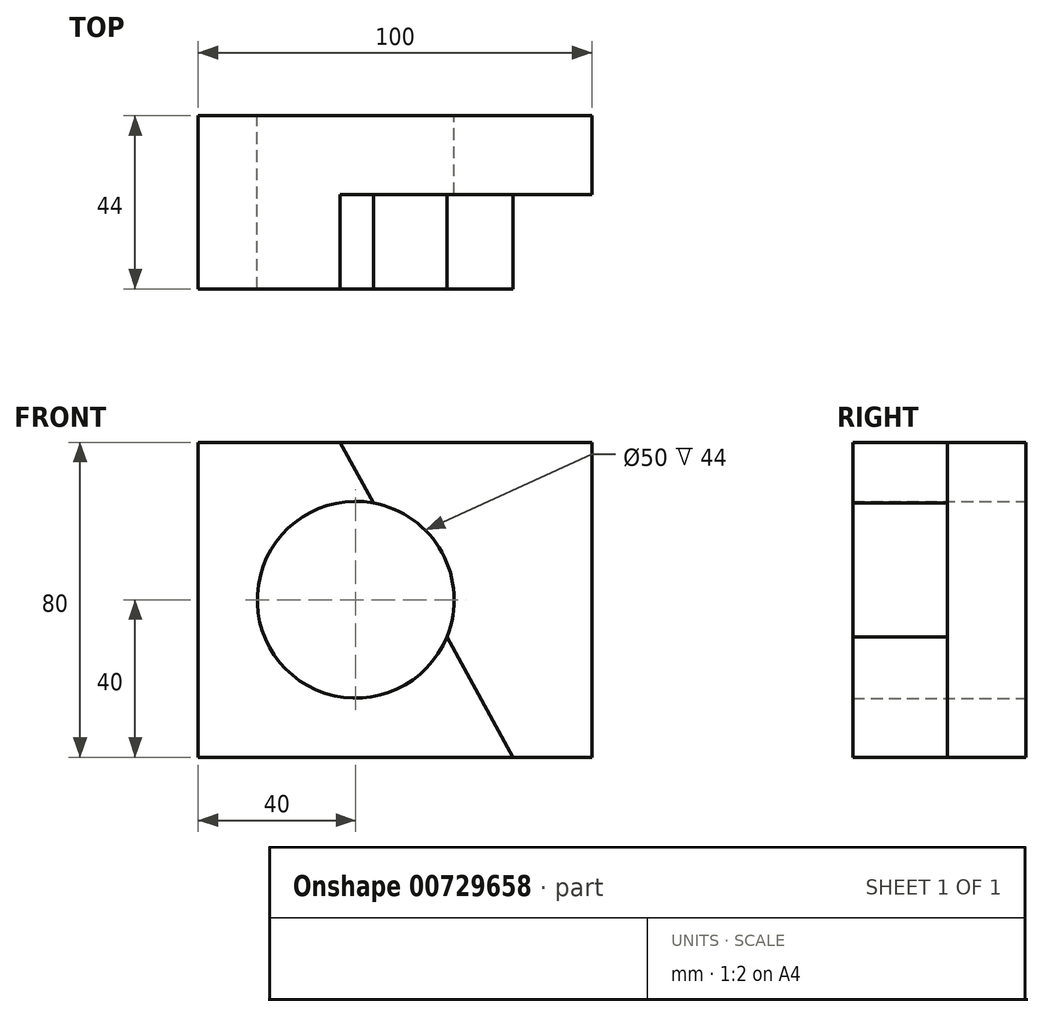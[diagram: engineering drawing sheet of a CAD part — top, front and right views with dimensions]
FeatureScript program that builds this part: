
annotation { "Feature Type Name" : "Feature", "Feature Type Description" : "" }
export const myFeature = defineFeature(function(context is Context, id is Id, definition is map)
    precondition{}
    {
        {
            var Q0;
            Q0=qCreatedBy(makeId("Front.planeOp"),FACE);
            var sketch = newSketch(context, id + "F0", { "sketchPlane" : qUnion([Q0])});
            skLineSegment(sketch, "E0.bottom", {"start": v(0, 0) * mm, "end": v(100, 0) * mm});
            skLineSegment(sketch, "E0.top", {"start": v(0, 80) * mm, "end": v(100, 80) * mm});
            skLineSegment(sketch, "E0.left", {"start": v(0, 0) * mm, "end": v(0, 80) * mm});
            skLineSegment(sketch, "E0.right", {"start": v(100, 0) * mm, "end": v(100, 80) * mm});
            skCircle(sketch, "E1", {"center": v(40, 40) * mm, "radius": 25 * mm});
            skSolve(sketch);
        }
        {
            var Q0;
            Q0 = qSketchRegion(id + "F0", true);
            extrude(context, id + "F1", {"entities" : qUnion([Q0]), "depth" : 44 * mm, "offsetDistance" : 25 * mm});
        }
        {
            var Q0;
            Q0=makeQuery(id+"F1.opExtrude","CAP_FACE",FACE,{"disambiguationData":[OSD([sQuery(id+"F0.wireOp",EDGE,"E0.bottom"),sQuery(id+"F0.wireOp",EDGE,"E0.top"),sQuery(id+"F0.wireOp",EDGE,"E0.left"),sQuery(id+"F0.wireOp",EDGE,"E0.right"),sQuery(id+"F0.wireOp",EDGE,"E1")])],"isStart":false});
            var sketch = newSketch(context, id + "F2", { "sketchPlane" : qUnion([Q0])});
            skLineSegment(sketch, "E2", {"start": v(36, 80) * mm, "end": v(100, 80) * mm});
            skLineSegment(sketch, "E3", {"start": v(100, 80) * mm, "end": v(100, 0) * mm});
            skLineSegment(sketch, "E4", {"start": v(100, 0) * mm, "end": v(80, 0) * mm});
            skLineSegment(sketch, "E5", {"start": v(80, 0) * mm, "end": v(36, 80) * mm});
            skSolve(sketch);
        }
        {
            var Q0;
            Q0 = qSketchRegion(id + "F2", true);
            extrude(context, id + "F3", {"entities" : qUnion([Q0]), "operationType" : NewBodyOperationType.REMOVE, "oppositeDirection" : true, "depth" : 24 * mm, "offsetDistance" : 25 * mm});
        }
    });
